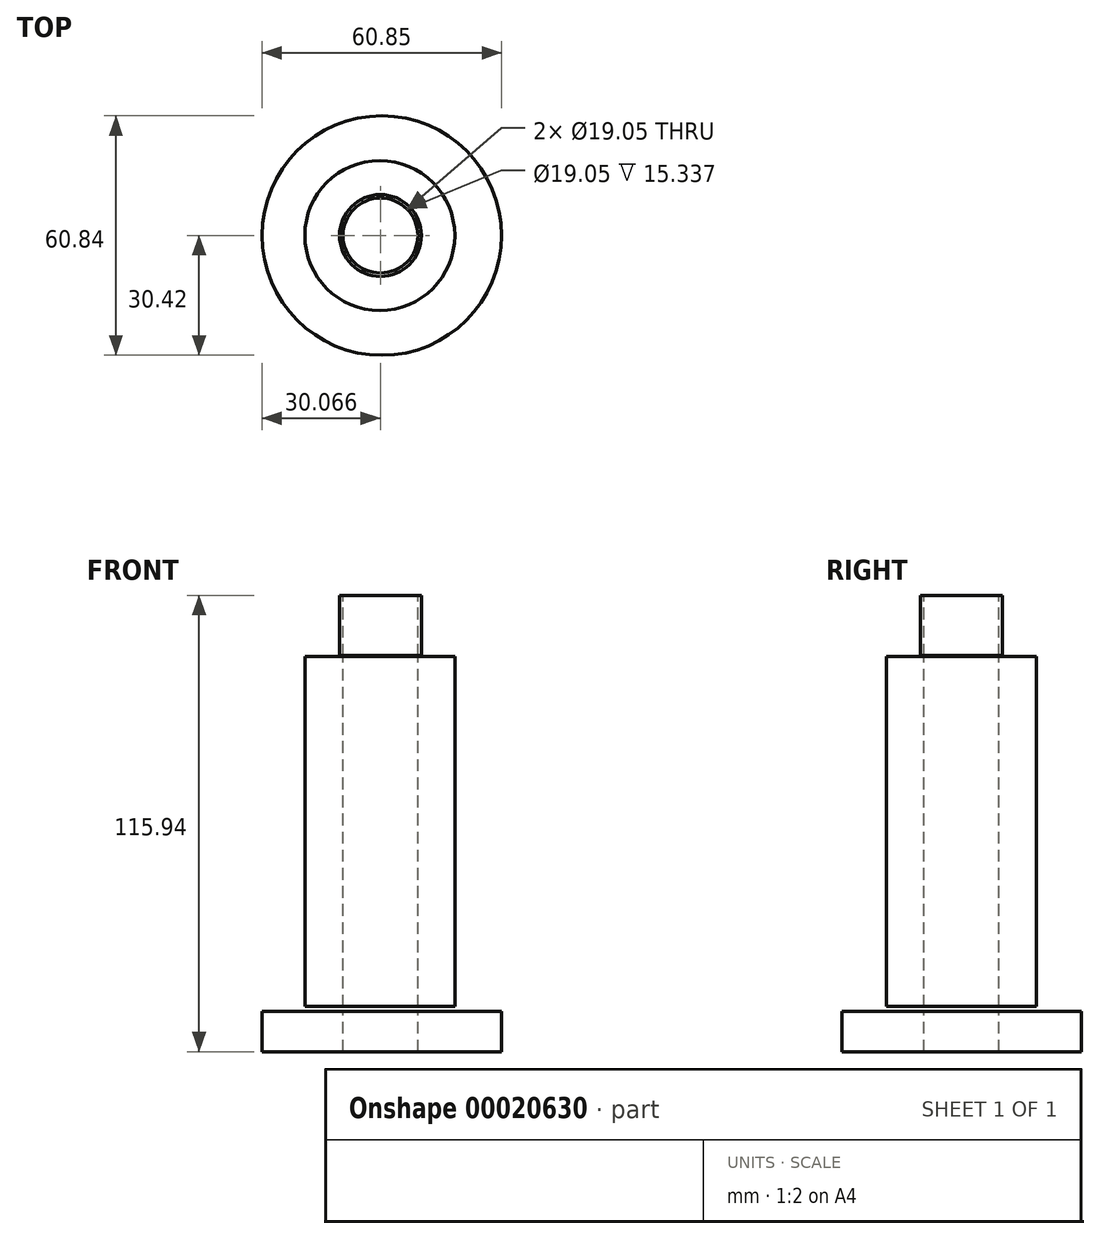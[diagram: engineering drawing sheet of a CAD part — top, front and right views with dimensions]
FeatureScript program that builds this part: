
annotation { "Feature Type Name" : "Feature", "Feature Type Description" : "" }
export const myFeature = defineFeature(function(context is Context, id is Id, definition is map)
    precondition{}
    {
        {
            var Q0;
            Q0=qCreatedBy(makeId("Front.planeOp"),FACE);
            var sketch = newSketch(context, id + "F0", { "sketchPlane" : qUnion([Q0])});
            skLineSegment(sketch, "E0.bottom", {"start": v(-37.3, 42.84) * mm, "end": v(-18.25, 42.84) * mm});
            skLineSegment(sketch, "E0.top", {"start": v(-37.3, -46.06) * mm, "end": v(-18.25, -46.06) * mm});
            skLineSegment(sketch, "E0.left", {"start": v(-37.3, 42.84) * mm, "end": v(-37.3, -46.06) * mm});
            skLineSegment(sketch, "E0.right", {"start": v(-18.25, 42.84) * mm, "end": v(-18.25, -46.06) * mm});
            skLineSegment(sketch, "E1.bottom", {"start": v(-22.58, 42.84) * mm, "end": v(-38.57, 42.84) * mm});
            skLineSegment(sketch, "E1.top", {"start": v(-22.58, 57.93) * mm, "end": v(-38.57, 57.93) * mm});
            skLineSegment(sketch, "E1.left", {"start": v(-22.58, 42.84) * mm, "end": v(-22.58, 57.93) * mm});
            skLineSegment(sketch, "E1.right", {"start": v(-38.57, 42.84) * mm, "end": v(-38.57, 57.93) * mm});
            skLineSegment(sketch, "E2.bottom", {"start": v(-23.57, -46.06) * mm, "end": v(-9.18, -46.06) * mm});
            skLineSegment(sketch, "E2.top", {"start": v(-23.57, -55.2) * mm, "end": v(-9.18, -55.2) * mm});
            skLineSegment(sketch, "E2.left", {"start": v(-23.57, -46.06) * mm, "end": v(-23.57, -55.2) * mm});
            skLineSegment(sketch, "E2.right", {"start": v(-9.18, -46.06) * mm, "end": v(-9.18, -55.2) * mm});
            skSolve(sketch);
        }
        {
            var Q0;
            Q0=makeQuery(id+"F0.imprint","IMPRINT",FACE,{"disambiguationData":[TD([[makeQuery(id+"F0.imprint","IMPRINT",EDGE,{"derivedFrom":sQuery(id+"F0.wireOp",EDGE,"E0.bottom")}),-1.0]])]});
            var Q1;
            Q1=sQuery(id+"F0.wireOp",EDGE,"E0.right");
            revolve(context, id + "F1", {"entities" : qUnion([Q0]), "axis" : qUnion([Q1]), "revolveType" : RevolveType.FULL});
        }
        {
            var Q0;
            Q0=qCreatedBy(makeId("Front.planeOp"),FACE);
            var sketch = newSketch(context, id + "F2", { "sketchPlane" : qUnion([Q0])});
            skLineSegment(sketch, "E3.bottom", {"start": v(-18.1, 43.06) * mm, "end": v(-28.48, 43.06) * mm});
            skLineSegment(sketch, "E3.top", {"start": v(-18.1, 58.4) * mm, "end": v(-28.48, 58.4) * mm});
            skLineSegment(sketch, "E3.left", {"start": v(-18.1, 43.06) * mm, "end": v(-18.1, 58.4) * mm});
            skLineSegment(sketch, "E3.right", {"start": v(-28.48, 43.06) * mm, "end": v(-28.48, 58.4) * mm});
            skSolve(sketch);
        }
        {
            var Q0;
            Q0=makeQuery(id+"F2.imprint","IMPRINT",FACE,{"disambiguationData":[TD([[makeQuery(id+"F2.imprint","IMPRINT",EDGE,{"derivedFrom":sQuery(id+"F2.wireOp",EDGE,"E3.bottom")}),-1.0]])]});
            var Q1;
            Q1=sQuery(id+"F2.wireOp",EDGE,"E3.left");
            revolve(context, id + "F3", {"entities" : qUnion([Q0]), "axis" : qUnion([Q1]), "revolveType" : RevolveType.FULL});
        }
        {
            var Q0;
            Q0=qCreatedBy(makeId("Front.planeOp"),FACE);
            var sketch = newSketch(context, id + "F4", { "sketchPlane" : qUnion([Q0])});
            skLineSegment(sketch, "E4.bottom", {"start": v(-17.73, -47.33) * mm, "end": v(-48.16, -47.33) * mm});
            skLineSegment(sketch, "E4.top", {"start": v(-17.73, -57.54) * mm, "end": v(-48.16, -57.54) * mm});
            skLineSegment(sketch, "E4.left", {"start": v(-17.73, -47.33) * mm, "end": v(-17.73, -57.54) * mm});
            skLineSegment(sketch, "E4.right", {"start": v(-48.16, -47.33) * mm, "end": v(-48.16, -57.54) * mm});
            skSolve(sketch);
        }
        {
            var Q0;
            Q0=makeQuery(id+"F4.imprint","IMPRINT",FACE,{"disambiguationData":[TD([[makeQuery(id+"F4.imprint","IMPRINT",EDGE,{"derivedFrom":sQuery(id+"F4.wireOp",EDGE,"E4.bottom")}),1.0]])]});
            var Q1;
            Q1=sQuery(id+"F4.wireOp",EDGE,"E4.left");
            revolve(context, id + "F5", {"entities" : qUnion([Q0]), "axis" : qUnion([Q1]), "revolveType" : RevolveType.FULL});
        }
        {
            var Q0;
            Q0=makeQuery(id+"F3.opRevolve","SWEPT_FACE",FACE,{"disambiguationData":[OSD([sQuery(id+"F2.wireOp",EDGE,"E3.top")])]});
            var sketch = newSketch(context, id + "F6", { "sketchPlane" : qUnion([Q0])});
            skCircle(sketch, "E5", {"center": v(-18.1, 0) * mm, "radius": 9.53 * mm});
            skSolve(sketch);
        }
        {
            var Q0;
            Q0 = qSketchRegion(id + "F6", true);
            extrude(context, id + "F7", {"entities" : qUnion([Q0]), "operationType" : NewBodyOperationType.REMOVE, "endBound" : BoundingType.THROUGH_ALL, "oppositeDirection" : true, "depth" : 25.4 * mm});
        }
    });
